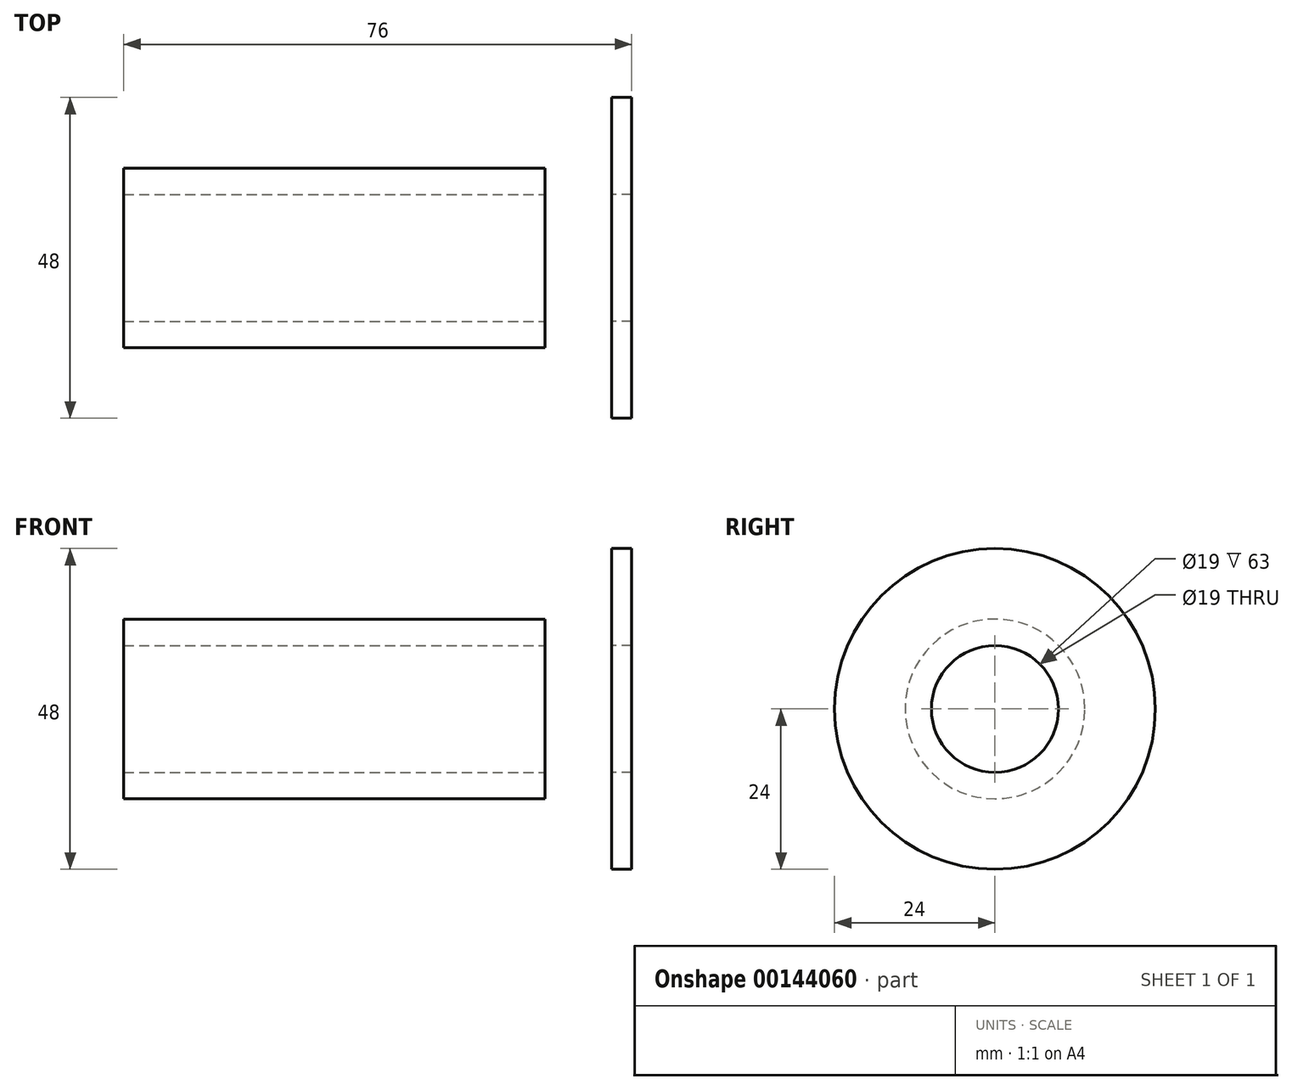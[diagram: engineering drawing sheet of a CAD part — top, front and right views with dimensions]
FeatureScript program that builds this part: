
annotation { "Feature Type Name" : "Feature", "Feature Type Description" : "" }
export const myFeature = defineFeature(function(context is Context, id is Id, definition is map)
    precondition{}
    {
        {
            var Q0;
            Q0=qCreatedBy(makeId("Right.planeOp"),FACE);
            var sketch = newSketch(context, id + "F0", { "sketchPlane" : qUnion([Q0])});
            skCircle(sketch, "E0", {"center": v(0, 0) * mm, "radius": 24 * mm});
            skCircle(sketch, "E1", {"center": v(0, 0) * mm, "radius": 9.5 * mm});
            skSolve(sketch);
        }
        {
            var Q0;
            Q0=makeQuery(id+"F0.imprint","IMPRINT",FACE,{"disambiguationData":[TD([[makeQuery(id+"F0.imprint","IMPRINT",EDGE,{"derivedFrom":sQuery(id+"F0.wireOp",EDGE,"E0")}),1.0]])]});
            extrude(context, id + "F1", {"entities" : qUnion([Q0]), "depth" : 3 * mm});
        }
        {
            var Q0;
            Q0=makeQuery(id+"F1.opExtrude","CAP_FACE",FACE,{"disambiguationData":[OSD([sQuery(id+"F0.wireOp",EDGE,"E0"),sQuery(id+"F0.wireOp",EDGE,"E1")])],"isStart":true});
            cPlane(context, id + "F2", {"entities" : qUnion([Q0]), "cplaneType" : CPlaneType.OFFSET, "offset" : 10 * mm, "width" : 150 * mm, "height" : 150 * mm});
        }
        {
            var Q0;
            Q0=qCreatedBy(id+"F2.planeOp",FACE);
            var sketch = newSketch(context, id + "F3", { "sketchPlane" : qUnion([Q0])});
            skCircle(sketch, "E2", {"center": v(0, 0) * mm, "radius": 9.5 * mm});
            skCircle(sketch, "E3", {"center": v(0, 0) * mm, "radius": 13.45 * mm});
            skSolve(sketch);
        }
        {
            var Q0;
            Q0=makeQuery(id+"F3.imprint","IMPRINT",FACE,{"disambiguationData":[TD([[makeQuery(id+"F3.imprint","IMPRINT",EDGE,{"derivedFrom":sQuery(id+"F3.wireOp",EDGE,"E2")}),-1.0]])]});
            extrude(context, id + "F4", {"entities" : qUnion([Q0]), "depth" : 63 * mm});
        }
    });
